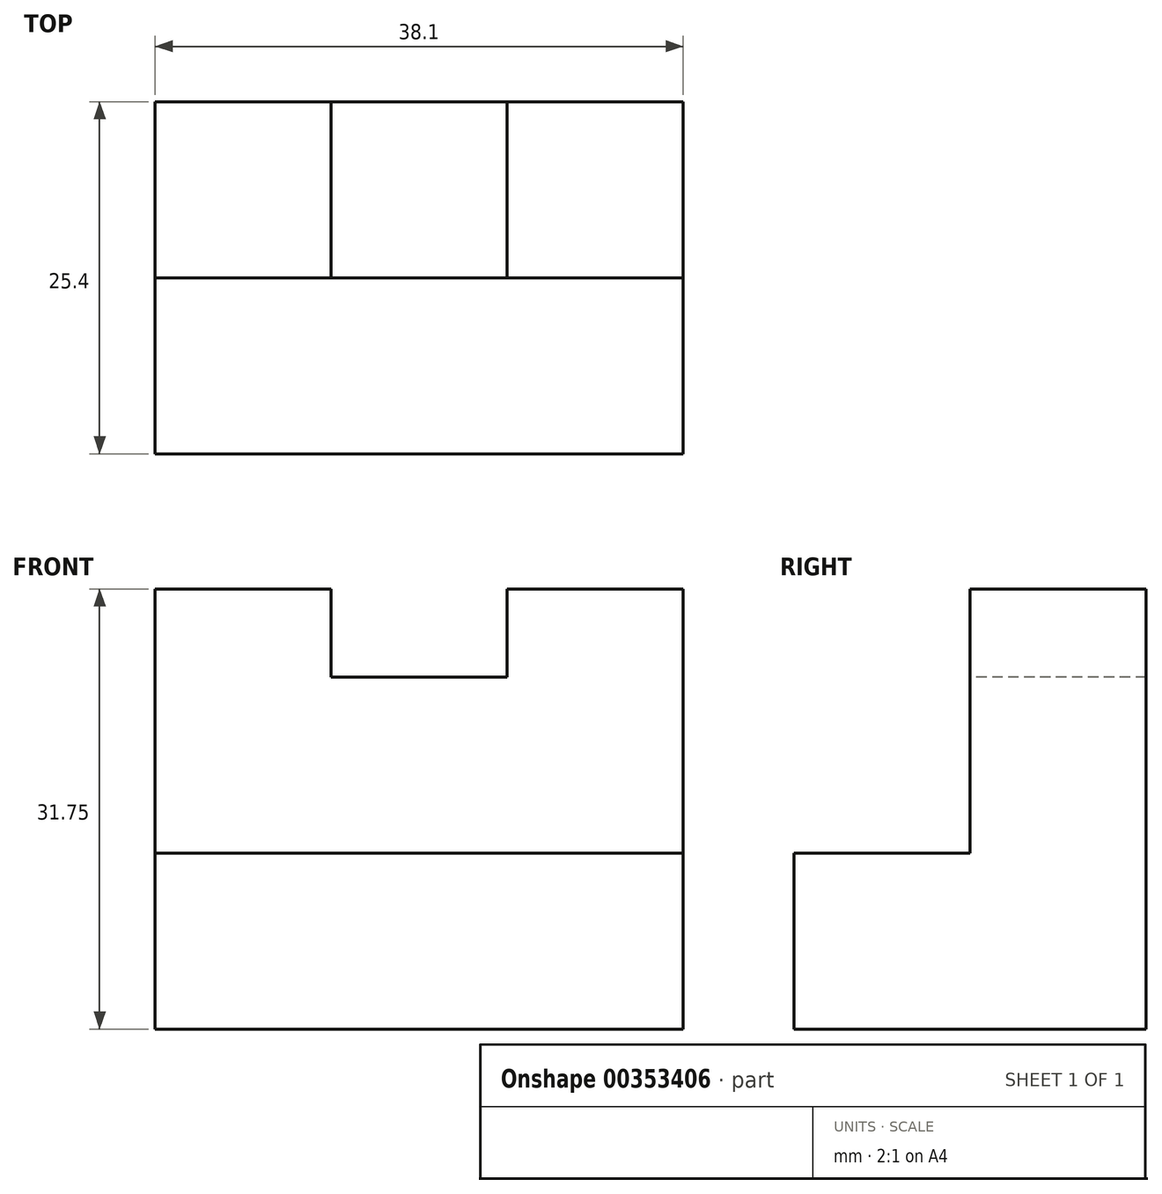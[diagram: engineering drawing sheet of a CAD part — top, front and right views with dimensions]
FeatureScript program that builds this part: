
annotation { "Feature Type Name" : "Feature", "Feature Type Description" : "" }
export const myFeature = defineFeature(function(context is Context, id is Id, definition is map)
    precondition{}
    {
        {
            var Q0;
            Q0=qCreatedBy(makeId("Right.planeOp"),FACE);
            var sketch = newSketch(context, id + "F0", { "sketchPlane" : qUnion([Q0])});
            skLineSegment(sketch, "E0", {"start": v(0, 0) * mm, "end": v(0, 12.7) * mm});
            skLineSegment(sketch, "E1", {"start": v(0, 12.7) * mm, "end": v(12.7, 12.7) * mm});
            skLineSegment(sketch, "E2", {"start": v(12.7, 12.7) * mm, "end": v(12.7, 31.75) * mm});
            skLineSegment(sketch, "E3", {"start": v(12.7, 31.75) * mm, "end": v(25.4, 31.75) * mm});
            skLineSegment(sketch, "E4", {"start": v(25.4, 31.75) * mm, "end": v(25.4, 0) * mm});
            skLineSegment(sketch, "E5", {"start": v(25.4, 0) * mm, "end": v(25.4, 0) * mm});
            skLineSegment(sketch, "E6", {"start": v(25.4, 0) * mm, "end": v(0, 0) * mm});
            skSolve(sketch);
        }
        {
            var Q0;
            Q0 = qSketchRegion(id + "F0", true);
            extrude(context, id + "F1", {"entities" : qUnion([Q0]), "depth" : 38.1 * mm});
        }
        {
            var Q0;
            Q0=makeQuery(id+"F1.opExtrude","SWEPT_FACE",FACE,{"disambiguationData":[OSD([sQuery(id+"F0.wireOp",EDGE,"E2")])]});
            var sketch = newSketch(context, id + "F2", { "sketchPlane" : qUnion([Q0])});
            skLineSegment(sketch, "E7", {"start": v(0, 31.75) * mm, "end": v(12.7, 31.75) * mm});
            skLineSegment(sketch, "E8", {"start": v(12.7, 31.75) * mm, "end": v(12.7, 25.4) * mm});
            skLineSegment(sketch, "E9", {"start": v(12.7, 25.4) * mm, "end": v(25.4, 25.4) * mm});
            skLineSegment(sketch, "E10", {"start": v(25.4, 25.4) * mm, "end": v(25.4, 31.75) * mm});
            skLineSegment(sketch, "E11", {"start": v(25.4, 31.75) * mm, "end": v(38.1, 31.75) * mm});
            skLineSegment(sketch, "E12", {"start": v(12.7, 31.75) * mm, "end": v(25.4, 31.75) * mm});
            skSolve(sketch);
        }
        {
            var Q0;
            Q0 = qSketchRegion(id + "F2", true);
            extrude(context, id + "F3", {"entities" : qUnion([Q0]), "operationType" : NewBodyOperationType.REMOVE, "oppositeDirection" : true, "depth" : 25.4 * mm});
        }
    });
